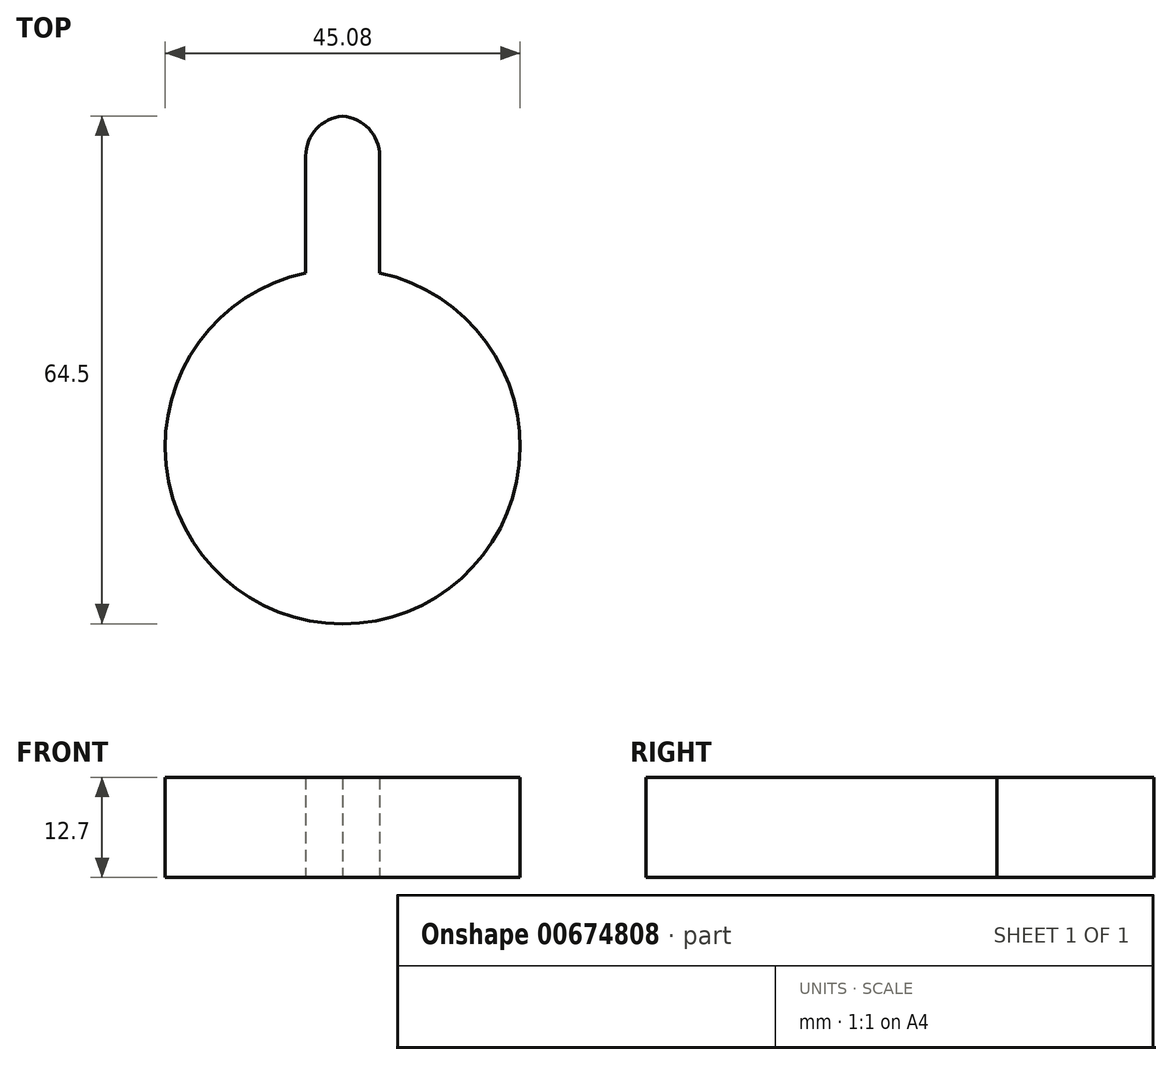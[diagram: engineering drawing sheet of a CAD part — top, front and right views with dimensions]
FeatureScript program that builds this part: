
annotation { "Feature Type Name" : "Feature", "Feature Type Description" : "" }
export const myFeature = defineFeature(function(context is Context, id is Id, definition is map)
    precondition{}
    {
        {
            var Q0;
            Q0=qCreatedBy(makeId("Top.planeOp"),FACE);
            var sketch = newSketch(context, id + "F0", { "sketchPlane" : qUnion([Q0])});
            skCircle(sketch, "E0", {"center": v(0, 0) * mm, "radius": 22.54 * mm});
            skLineSegment(sketch, "E1", {"start": v(-4.7, 22.05) * mm, "end": v(-4.7, 36.9) * mm});
            skLineSegment(sketch, "E2.MirrorCS", {"start": v(4.7, 22.05) * mm, "end": v(4.7, 36.9) * mm});
            skLineSegment(sketch, "E3", {"start": v(-0.39, 41.98) * mm, "end": v(0.39, 41.98) * mm});
            skPoint(sketch, "E4.visualSharp", {"position": v(4.7, 41.98) * mm});
            skArc(sketch, "E4.filletArc", {"start": v(4.7, 36.9) * mm, "mid": v(3.2, 40.49) * mm, "end": v(-0.39, 41.98) * mm});
            skPoint(sketch, "E5.visualSharp", {"position": v(-4.7, 41.98) * mm});
            skArc(sketch, "E5.filletArc", {"start": v(0.39, 41.98) * mm, "mid": v(-3.2, 40.49) * mm, "end": v(-4.7, 36.9) * mm});
            skSolve(sketch);
        }
        {
            var Q0;
            {var subQ1=sQuery(id+"F0.wireOp",EDGE,"E1");Q0=makeQuery(id+"F0.imprint","IMPRINT",FACE,{"disambiguationData":[TD([[makeQuery(id+"F0.imprint","IMPRINT",EDGE,{"derivedFrom":subQ1}),-1.0]])]});}
            var Q1;
            {var subQ0=sQuery(id+"F0.wireOp",EDGE,"E0");var subQ1=makeQuery(id+"F0.imprint","INTERSECT",VERTEX,{"derivedFrom":[subQ0,sQuery(id+"F0.wireOp",EDGE,"E1")]});Q1=makeQuery(id+"F0.imprint","IMPRINT",FACE,{"disambiguationData":[TD([[makeQuery(id+"F0.imprint","IMPRINT",EDGE,{"disambiguationData":[TD([[subQ1,1.0]])],"derivedFrom":subQ0}),1.0]])]});}
            extrude(context, id + "F1", {"entities" : qUnion([Q0, Q1]), "depth" : 12.7 * mm, "offsetDistance" : 25.4 * mm});
        }
    });
